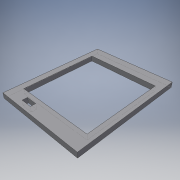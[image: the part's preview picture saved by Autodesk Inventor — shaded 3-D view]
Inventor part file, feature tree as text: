
AUTODESK INVENTOR PART (.ipt)
format: ipt  version: 2016 (Build 200138000, 138)  size: 113,152 bytes
history: native  units: in
note: dims shown in document units (in); Inventor stores cm internally (conversion verified against a paired STEP export)
features: extrude x3, sketch x3
ambient origin geometry x8: Origin, YZ Plane, XZ Plane, XY Plane, X Axis, Y Axis, Z Axis, Center Point
bodies: Solid1 (feature_tree)
feature tree (6):
  extrude  "Extrusion1"  Depth=16.0in
  extrude  "Extrusion2"  Depth=14.5in
  extrude  "Extrusion3"  Depth=1.0in TaperAngle=0.0deg
  sketch  "Sketch1"  dims[d0=20.0in d1=16.0in]
  sketch  "Sketch2"  dims[d2=1.0in d3=0.0in d4=14.5in]
  sketch  "Sketch3"  dims[d5=13.5in d6=1.0in d7=0.0in d9=3.5in d10=2.0in d11=1.0in d12=0.0in d13=0.9in d14=1.0in]
